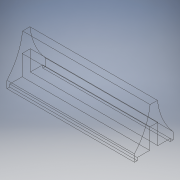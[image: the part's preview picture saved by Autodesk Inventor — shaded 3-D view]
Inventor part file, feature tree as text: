
AUTODESK INVENTOR PART (.ipt)
format: ipt  version: 2022.2 (Build 262287010, 287A)  size: 316,928 bytes
history: native  units: in
note: dims shown in document units (in); Inventor stores cm internally (conversion verified against a paired STEP export)
features: revolve x2, other x1, direct_edit x1
ambient origin geometry x8: Origin, YZ Plane, XZ Plane, XY Plane, X Axis, Y Axis, Z Axis, Center Point
bodies: Solid1 (feature_tree)
feature tree (4):
  other  "Upper Mull (2)"
  direct_edit  "Direct Edit1"
  revolve  "Rotate1"  [1 undecoded]
  revolve  "Rotate2"  Angle=180.0deg
note: 1 required parameter value undecoded (feature->parameter linkage not recoverable at this tier; creation-order binding heuristic only, values carry confidence <= 0.55)
